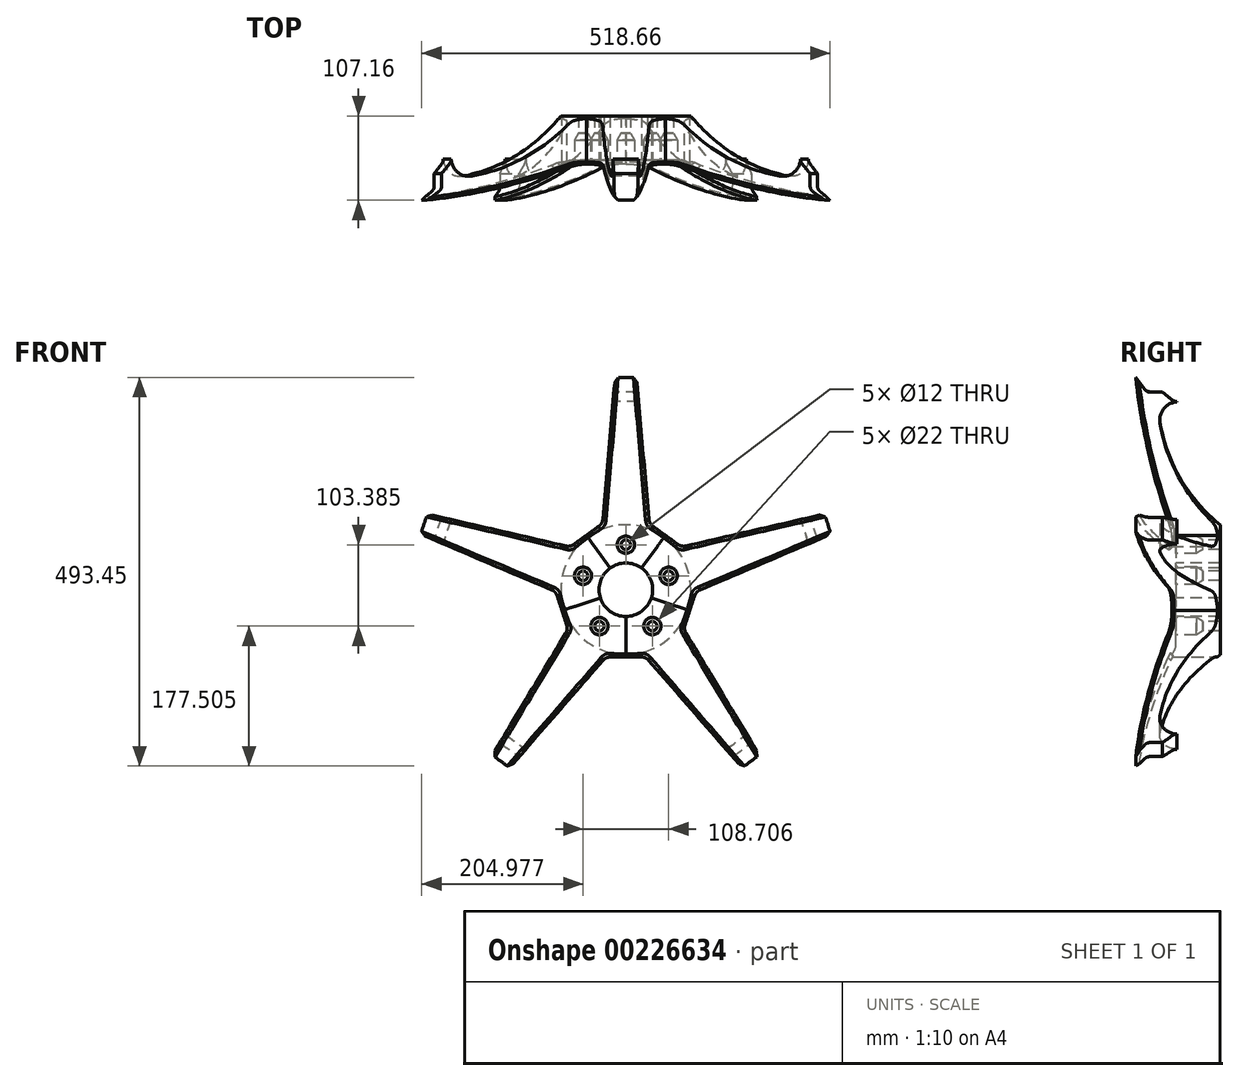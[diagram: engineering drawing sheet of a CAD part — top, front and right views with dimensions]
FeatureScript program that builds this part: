
annotation { "Feature Type Name" : "Feature", "Feature Type Description" : "" }
export const myFeature = defineFeature(function(context is Context, id is Id, definition is map)
    precondition{}
    {
        {
            var Q0;
            Q0=qCreatedBy(makeId("Right.planeOp"),FACE);
            var sketch = newSketch(context, id + "F0", { "sketchPlane" : qUnion([Q0])});
            skLineSegment(sketch, "E0", {"start": v(-123.86, 254) * mm, "end": v(-109.52, 254) * mm, "construction": true});
            skLineSegment(sketch, "E1", {"start": v(0, 0) * mm, "end": v(0, 254) * mm, "construction": true});
            skPoint(sketch, "E1.endSnap0", {"position": v(0, 254) * mm});
            skLineSegment(sketch, "E2", {"start": v(-140.14, 271.25) * mm, "end": v(-128.9, 256.5) * mm});
            skLineSegment(sketch, "E3", {"start": v(-105.46, 252.53) * mm, "end": v(-94.14, 243.13) * mm});
            skLineSegment(sketch, "E4", {"start": v(-89.81, 241.67) * mm, "end": v(77.91, 248.76) * mm});
            skLineSegment(sketch, "E5", {"start": v(79.7, 249.1) * mm, "end": v(93.05, 253.66) * mm});
            skLineSegment(sketch, "E6", {"start": v(95.1, 254) * mm, "end": v(123.47, 254) * mm});
            skLineSegment(sketch, "E7", {"start": v(128.86, 257) * mm, "end": v(138.45, 272.41) * mm});
            skPoint(sketch, "E8.visualSharp", {"position": v(-127, 254) * mm});
            skArc(sketch, "E8.filletArc", {"start": v(-128.9, 256.5) * mm, "mid": v(-126.67, 254.66) * mm, "end": v(-123.86, 254) * mm});
            skPoint(sketch, "E9.newPointA", {"position": v(127, 254) * mm});
            skArc(sketch, "E9.filletArc", {"start": v(-105.46, 252.53) * mm, "mid": v(-107.36, 253.62) * mm, "end": v(-109.52, 254) * mm});
            skPoint(sketch, "E10.visualSharp", {"position": v(-92.26, 241.57) * mm});
            skArc(sketch, "E10.filletArc", {"start": v(-94.14, 243.13) * mm, "mid": v(-92.11, 242) * mm, "end": v(-89.81, 241.67) * mm});
            skPoint(sketch, "E11.visualSharp", {"position": v(78.83, 248.8) * mm});
            skArc(sketch, "E11.filletArc", {"start": v(77.91, 248.76) * mm, "mid": v(78.82, 248.86) * mm, "end": v(79.7, 249.1) * mm});
            skPoint(sketch, "E12.visualSharp", {"position": v(94.04, 254) * mm});
            skArc(sketch, "E12.filletArc", {"start": v(95.1, 254) * mm, "mid": v(94.06, 253.91) * mm, "end": v(93.05, 253.66) * mm});
            skArc(sketch, "E13.filletArc", {"start": v(123.47, 254) * mm, "mid": v(126.56, 254.8) * mm, "end": v(128.86, 257) * mm});
            skSolve(sketch);
        }
        {
            var Q0;
            Q0=qCreatedBy(makeId("Right.planeOp"),FACE);
            var sketch = newSketch(context, id + "F1", { "sketchPlane" : qUnion([Q0])});
            skLineSegment(sketch, "E14.0", {"start": v(131.02, 255.65) * mm, "end": v(140.61, 271.07) * mm});
            skLineSegment(sketch, "E14.1", {"start": v(-108.14, 251.46) * mm, "end": v(-95.76, 241.18) * mm});
            skLineSegment(sketch, "E14.2", {"start": v(-123.86, 251.46) * mm, "end": v(-108.14, 251.46) * mm});
            skArc(sketch, "E14.3", {"start": v(-130.93, 254.96) * mm, "mid": v(-127.8, 252.38) * mm, "end": v(-123.86, 251.46) * mm});
            skLineSegment(sketch, "E14.4", {"start": v(-142.16, 269.7) * mm, "end": v(-130.93, 254.96) * mm});
            skArc(sketch, "E14.5", {"start": v(-95.76, 241.18) * mm, "mid": v(-92.93, 239.6) * mm, "end": v(-89.7, 239.13) * mm});
            skLineSegment(sketch, "E14.6", {"start": v(-89.7, 239.13) * mm, "end": v(78.02, 246.22) * mm});
            skArc(sketch, "E14.7", {"start": v(78.02, 246.22) * mm, "mid": v(79.29, 246.37) * mm, "end": v(80.52, 246.7) * mm});
            skLineSegment(sketch, "E14.8", {"start": v(80.52, 246.7) * mm, "end": v(94.47, 251.46) * mm});
            skLineSegment(sketch, "E14.9", {"start": v(94.47, 251.46) * mm, "end": v(123.47, 251.46) * mm});
            skArc(sketch, "E14.10", {"start": v(123.47, 251.46) * mm, "mid": v(127.79, 252.58) * mm, "end": v(131.02, 255.65) * mm});
            skLineSegment(sketch, "E15.0", {"start": v(-105.46, 252.53) * mm, "end": v(-94.14, 243.13) * mm});
            skLineSegment(sketch, "E15.1", {"start": v(-140.14, 271.25) * mm, "end": v(-128.9, 256.5) * mm});
            skArc(sketch, "E15.2", {"start": v(-128.9, 256.5) * mm, "mid": v(-126.67, 254.66) * mm, "end": v(-123.86, 254) * mm});
            skLineSegment(sketch, "E15.3", {"start": v(-123.86, 254) * mm, "end": v(-109.52, 254) * mm});
            skArc(sketch, "E15.4", {"start": v(-105.46, 252.53) * mm, "mid": v(-107.36, 253.62) * mm, "end": v(-109.52, 254) * mm});
            skPoint(sketch, "E15.5", {"position": v(-92.26, 241.57) * mm});
            skArc(sketch, "E15.6", {"start": v(-94.14, 243.13) * mm, "mid": v(-92.11, 242) * mm, "end": v(-89.81, 241.67) * mm});
            skLineSegment(sketch, "E15.7", {"start": v(-89.81, 241.67) * mm, "end": v(77.91, 248.76) * mm});
            skLineSegment(sketch, "E15.8", {"start": v(128.86, 257) * mm, "end": v(138.45, 272.41) * mm});
            skArc(sketch, "E15.9", {"start": v(123.47, 254) * mm, "mid": v(126.56, 254.8) * mm, "end": v(128.86, 257) * mm});
            skLineSegment(sketch, "E15.10", {"start": v(95.1, 254) * mm, "end": v(123.47, 254) * mm});
            skArc(sketch, "E15.11", {"start": v(95.1, 254) * mm, "mid": v(94.06, 253.91) * mm, "end": v(93.05, 253.66) * mm});
            skLineSegment(sketch, "E15.12", {"start": v(79.7, 249.1) * mm, "end": v(93.05, 253.66) * mm});
            skArc(sketch, "E15.13", {"start": v(77.91, 248.76) * mm, "mid": v(78.82, 248.86) * mm, "end": v(79.7, 249.1) * mm});
            skLineSegment(sketch, "E16", {"start": v(-140.14, 271.25) * mm, "end": v(-142.16, 269.7) * mm});
            skLineSegment(sketch, "E17", {"start": v(138.45, 272.41) * mm, "end": v(140.61, 271.07) * mm});
            skLineSegment(sketch, "E18", {"start": v(0, 0) * mm, "end": v(-132.17, 0) * mm, "construction": true});
            skSolve(sketch);
        }
        {
            var Q0;
            Q0=qCreatedBy(makeId("Right.planeOp"),FACE);
            var sketch = newSketch(context, id + "F2", { "sketchPlane" : qUnion([Q0])});
            skLineSegment(sketch, "E19", {"start": v(-35, 0) * mm, "end": v(-35, 116.08) * mm, "construction": true});
            skLineSegment(sketch, "E20", {"start": v(0, 34) * mm, "end": v(-35, 34) * mm, "construction": true});
            skLineSegment(sketch, "E21", {"start": v(0, 57.15) * mm, "end": v(-35, 57.15) * mm, "construction": true});
            skLineSegment(sketch, "E22", {"start": v(-35, 34) * mm, "end": v(-90.96, 34) * mm});
            skLineSegment(sketch, "E23", {"start": v(-35, 34) * mm, "end": v(-35, 82.55) * mm});
            skArc(sketch, "E24", {"start": v(-111.34, 212.33) * mm, "mid": v(-85.02, 140.47) * mm, "end": v(-35, 82.55) * mm});
            skArc(sketch, "E25", {"start": v(-89.7, 239.13) * mm, "mid": v(-106.58, 230.62) * mm, "end": v(-111.34, 212.33) * mm});
            skArc(sketch, "E26.0", {"start": v(-95.76, 241.18) * mm, "mid": v(-92.93, 239.6) * mm, "end": v(-89.7, 239.13) * mm});
            skLineSegment(sketch, "E26.1", {"start": v(-123.86, 251.46) * mm, "end": v(-108.14, 251.46) * mm});
            skLineSegment(sketch, "E26.2", {"start": v(-108.14, 251.46) * mm, "end": v(-95.76, 241.18) * mm});
            skArc(sketch, "E26.3", {"start": v(-130.93, 254.96) * mm, "mid": v(-127.8, 252.38) * mm, "end": v(-123.86, 251.46) * mm});
            skLineSegment(sketch, "E26.4", {"start": v(-142.16, 269.7) * mm, "end": v(-130.93, 254.96) * mm});
            skLineSegment(sketch, "E27", {"start": v(-90.96, 34) * mm, "end": v(-90.96, 68.2) * mm});
            skArc(sketch, "E28", {"start": v(-90.96, 68.2) * mm, "mid": v(-92.63, 76.26) * mm, "end": v(-97.37, 83) * mm});
            skArc(sketch, "E29", {"start": v(-142.16, 269.7) * mm, "mid": v(-126.3, 176.22) * mm, "end": v(-98.98, 85.42) * mm});
            skPoint(sketch, "E30.visualSharp", {"position": v(-98.42, 83.91) * mm});
            skArc(sketch, "E30.filletArc", {"start": v(-98.98, 85.42) * mm, "mid": v(-98.32, 84.11) * mm, "end": v(-97.37, 83) * mm});
            skLineSegment(sketch, "E31", {"start": v(-132.89, 0) * mm, "end": v(0, 0) * mm, "construction": true});
            skSolve(sketch);
        }
        {
            var Q0;
            Q0=qSketchRegion(id+"F2",true);
            var Q1;
            Q1=sQuery(id+"F2.wireOp",EDGE,"E31");
            revolve(context, id + "F3", {"entities" : qUnion([Q0]), "axis" : qUnion([Q1]), "revolveType" : RevolveType.FULL});
        }
        {
            var Q0;
            Q0=qCreatedBy(makeId("Front.planeOp"),FACE);
            var sketch = newSketch(context, id + "F4", { "sketchPlane" : qUnion([Q0])});
            skCircle(sketch, "E32", {"center": v(0, 0) * mm, "radius": 57.15 * mm, "construction": true});
            skLineSegment(sketch, "E33", {"start": v(0, 0) * mm, "end": v(0, 279.4) * mm, "construction": true});
            skCircle(sketch, "E34", {"center": v(0, 0) * mm, "radius": 279.4 * mm, "construction": true});
            skLineSegment(sketch, "E35", {"start": v(12.7, 279.11) * mm, "end": v(29.27, 89.72) * mm});
            skLineSegment(sketch, "E36", {"start": v(0, 0) * mm, "end": v(164.23, 226.04) * mm, "construction": true});
            skLineSegment(sketch, "E37", {"start": v(50.2, 69.1) * mm, "end": v(34.46, 80.55) * mm});
            skPoint(sketch, "E38.visualSharp", {"position": v(29.77, 83.96) * mm});
            skArc(sketch, "E38.filletArc", {"start": v(29.27, 89.72) * mm, "mid": v(30.87, 84.57) * mm, "end": v(34.46, 80.55) * mm});
            skArc(sketch, "E39.MirrorCS", {"start": v(76.28, 55.56) * mm, "mid": v(70.9, 55.5) * mm, "end": v(65.96, 57.66) * mm});
            skLineSegment(sketch, "E40.MirrorCS", {"start": v(261.53, 98.33) * mm, "end": v(76.28, 55.56) * mm});
            skLineSegment(sketch, "E41.MirrorCS", {"start": v(50.2, 69.1) * mm, "end": v(65.96, 57.66) * mm});
            skArc(sketch, "E42", {"start": v(261.53, 98.33) * mm, "mid": v(164.23, 226.04) * mm, "end": v(12.7, 279.11) * mm});
            skSolve(sketch);
        }
        {
            var Q0;
            Q0=qSketchRegion(id+"F4",true);
            extrude(context, id + "F5", {"entities" : qUnion([Q0]), "operationType" : NewBodyOperationType.REMOVE, "endBound" : BoundingType.THROUGH_ALL, "depth" : 25.4 * mm});
        }
        {
            var Q0;
            Q0=qCreatedBy(makeId("Front.planeOp"),FACE);
            var sketch = newSketch(context, id + "F6", { "sketchPlane" : qUnion([Q0])});
            skLineSegment(sketch, "E43", {"start": v(0, 0) * mm, "end": v(0, 283.46) * mm});
            skLineSegment(sketch, "E44", {"start": v(0, 0) * mm, "end": v(166.61, 229.32) * mm});
            skArc(sketch, "E45", {"start": v(0, 283.46) * mm, "mid": v(-87.6, -269.59) * mm, "end": v(166.61, 229.32) * mm});
            skSolve(sketch);
        }
        {
            var Q0;
            Q0=qSketchRegion(id+"F6",true);
            extrude(context, id + "F7", {"entities" : qUnion([Q0]), "operationType" : NewBodyOperationType.REMOVE, "endBound" : BoundingType.THROUGH_ALL, "depth" : 25.4 * mm});
        }
        {
            var Q0;
            Q0=makeQuery(id+"F5.boolean.opBoolean","INTERSECT",EDGE,{"derivedFrom":[makeQuery(id+"F3.opRevolve","SWEPT_FACE",FACE,{"disambiguationData":[OSD([sQuery(id+"F2.wireOp",EDGE,"E29")])]}),makeQuery(id+"F5.opExtrude","SWEPT_FACE",FACE,{"disambiguationData":[OSD([sQuery(id+"F4.wireOp",EDGE,"E35")])]})]});
            var Q1;
            Q1=makeQuery(id+"F5.boolean.opBoolean","INTERSECT",EDGE,{"derivedFrom":[makeQuery(id+"F3.opRevolve","SWEPT_FACE",FACE,{"disambiguationData":[OSD([sQuery(id+"F2.wireOp",EDGE,"E29")])]}),makeQuery(id+"F5.opExtrude","SWEPT_FACE",FACE,{"disambiguationData":[OSD([sQuery(id+"F4.wireOp",EDGE,"E38.filletArc")])]})]});
            var Q2;
            Q2=makeQuery(id+"F5.boolean.opBoolean","INTERSECT",EDGE,{"disambiguationData":[OD(0.0)],"derivedFrom":[makeQuery(id+"F3.opRevolve","SWEPT_FACE",FACE,{"disambiguationData":[OSD([sQuery(id+"F2.wireOp",EDGE,"E29")])]}),makeQuery(id+"F5.opExtrude","SWEPT_FACE",FACE,{"disambiguationData":[OSD([sQuery(id+"F4.wireOp",EDGE,"E37"),sQuery(id+"F4.wireOp",EDGE,"E41.MirrorCS")])]})]});
            chamfer(context, id + "F8", {"entities" : qUnion([Q0, Q1, Q2]), "width" : 3.8 * mm, "tangentPropagation" : true});
        }
        {
            var Q0;
            Q0=makeQuery(id+"F3.opRevolve","SWEPT_FACE",FACE,{"disambiguationData":[OSD([sQuery(id+"F2.wireOp",EDGE,"E27")])]});
            var sketch = newSketch(context, id + "F9", { "sketchPlane" : qUnion([Q0])});
            skCircle(sketch, "E46", {"center": v(0, 0) * mm, "radius": 57.15 * mm, "construction": true});
            skCircle(sketch, "E47", {"center": v(0, 57.15) * mm, "radius": 6 * mm});
            skSolve(sketch);
        }
        {
            var Q0;
            Q0=qSketchRegion(id+"F9",true);
            extrude(context, id + "F10", {"entities" : qUnion([Q0]), "operationType" : NewBodyOperationType.REMOVE, "endBound" : BoundingType.THROUGH_ALL, "oppositeDirection" : true, "depth" : 25.4 * mm});
        }
        {
            var Q0;
            Q0=makeQuery(id+"F3.opRevolve","SWEPT_FACE",FACE,{"disambiguationData":[OSD([sQuery(id+"F2.wireOp",EDGE,"E27")])]});
            var sketch = newSketch(context, id + "F11", { "sketchPlane" : qUnion([Q0])});
            skCircle(sketch, "E48", {"center": v(0, 57.15) * mm, "radius": 11 * mm});
            skSolve(sketch);
        }
        {
            var Q0;
            Q0=qSketchRegion(id+"F11",true);
            extrude(context, id + "F12", {"entities" : qUnion([Q0]), "operationType" : NewBodyOperationType.REMOVE, "oppositeDirection" : true, "depth" : 25.4 * mm});
        }
        {
            var Q0;
            Q0=makeQuery(id+"F12.boolean.opBoolean","INTERSECT",EDGE,{"derivedFrom":[makeQuery(id+"F10.boolean.opBoolean","COPY",FACE,{"derivedFrom":makeQuery(id+"F10.opExtrude","SWEPT_FACE",FACE,{"disambiguationData":[OSD([sQuery(id+"F9.wireOp",EDGE,"E47")])]})}),makeQuery(id+"F12.opExtrude","CAP_FACE",FACE,{"disambiguationData":[OSD([sQuery(id+"F11.wireOp",EDGE,"E48")])],"isStart":false})]});
            chamfer(context, id + "F13", {"entities" : qUnion([Q0]), "chamferType" : ChamferType.OFFSET_ANGLE, "width" : 5.08 * mm, "oppositeDirection" : false, "angle" : 60 * degree, "tangentPropagation" : true});
        }
        {
            var Q0;
            Q0=makeQuery(id+"F3.opRevolve","SWEPT_BODY",BODY,{"disambiguationData":[OSD([sQuery(id+"F2.wireOp",EDGE,"E22"),sQuery(id+"F2.wireOp",EDGE,"E23"),sQuery(id+"F2.wireOp",EDGE,"E24"),sQuery(id+"F2.wireOp",EDGE,"E25"),sQuery(id+"F2.wireOp",EDGE,"E26.0"),sQuery(id+"F2.wireOp",EDGE,"E26.1"),sQuery(id+"F2.wireOp",EDGE,"E26.2"),sQuery(id+"F2.wireOp",EDGE,"E26.3"),sQuery(id+"F2.wireOp",EDGE,"E26.4"),sQuery(id+"F2.wireOp",EDGE,"E27"),sQuery(id+"F2.wireOp",EDGE,"E28"),sQuery(id+"F2.wireOp",EDGE,"E29"),sQuery(id+"F2.wireOp",EDGE,"E30.filletArc")])]});
            var Q1;
            Q1=makeQuery(id+"F10.boolean.opBoolean","SPLIT",FACE,{"disambiguationData":[TD([makeQuery(id+"F3.opRevolve","SWEPT_FACE",FACE,{"disambiguationData":[OSD([sQuery(id+"F2.wireOp",EDGE,"E24")])]})])],"derivedFrom":makeQuery(id+"F7.boolean.opBoolean","COPY",FACE,{"derivedFrom":makeQuery(id+"F7.opExtrude","SWEPT_FACE",FACE,{"disambiguationData":[OSD([sQuery(id+"F6.wireOp",EDGE,"E43")])]})})});
            mirror(context, id + "F14", {"operationType" : NewBodyOperationType.ADD, "entities" : qUnion([Q0]), "mirrorPlane" : qUnion([Q1])});
        }
        {
            var Q0;
            Q0=makeQuery(id+"F3.opRevolve","SWEPT_BODY",BODY,{"disambiguationData":[OSD([sQuery(id+"F2.wireOp",EDGE,"E22"),sQuery(id+"F2.wireOp",EDGE,"E23"),sQuery(id+"F2.wireOp",EDGE,"E24"),sQuery(id+"F2.wireOp",EDGE,"E25"),sQuery(id+"F2.wireOp",EDGE,"E26.0"),sQuery(id+"F2.wireOp",EDGE,"E26.1"),sQuery(id+"F2.wireOp",EDGE,"E26.2"),sQuery(id+"F2.wireOp",EDGE,"E26.3"),sQuery(id+"F2.wireOp",EDGE,"E26.4"),sQuery(id+"F2.wireOp",EDGE,"E27"),sQuery(id+"F2.wireOp",EDGE,"E28"),sQuery(id+"F2.wireOp",EDGE,"E29"),sQuery(id+"F2.wireOp",EDGE,"E30.filletArc")])]});
            var Q1;
            Q1=sQuery(id+"F1.wireOp",EDGE,"E18");
            circularPattern(context, id + "F15", {"entities" : qUnion([Q0]), "axis" : qUnion([Q1]), "angle" : 360 * degree, "instanceCount" : 5, "equalSpace" : true});
        }
    });
